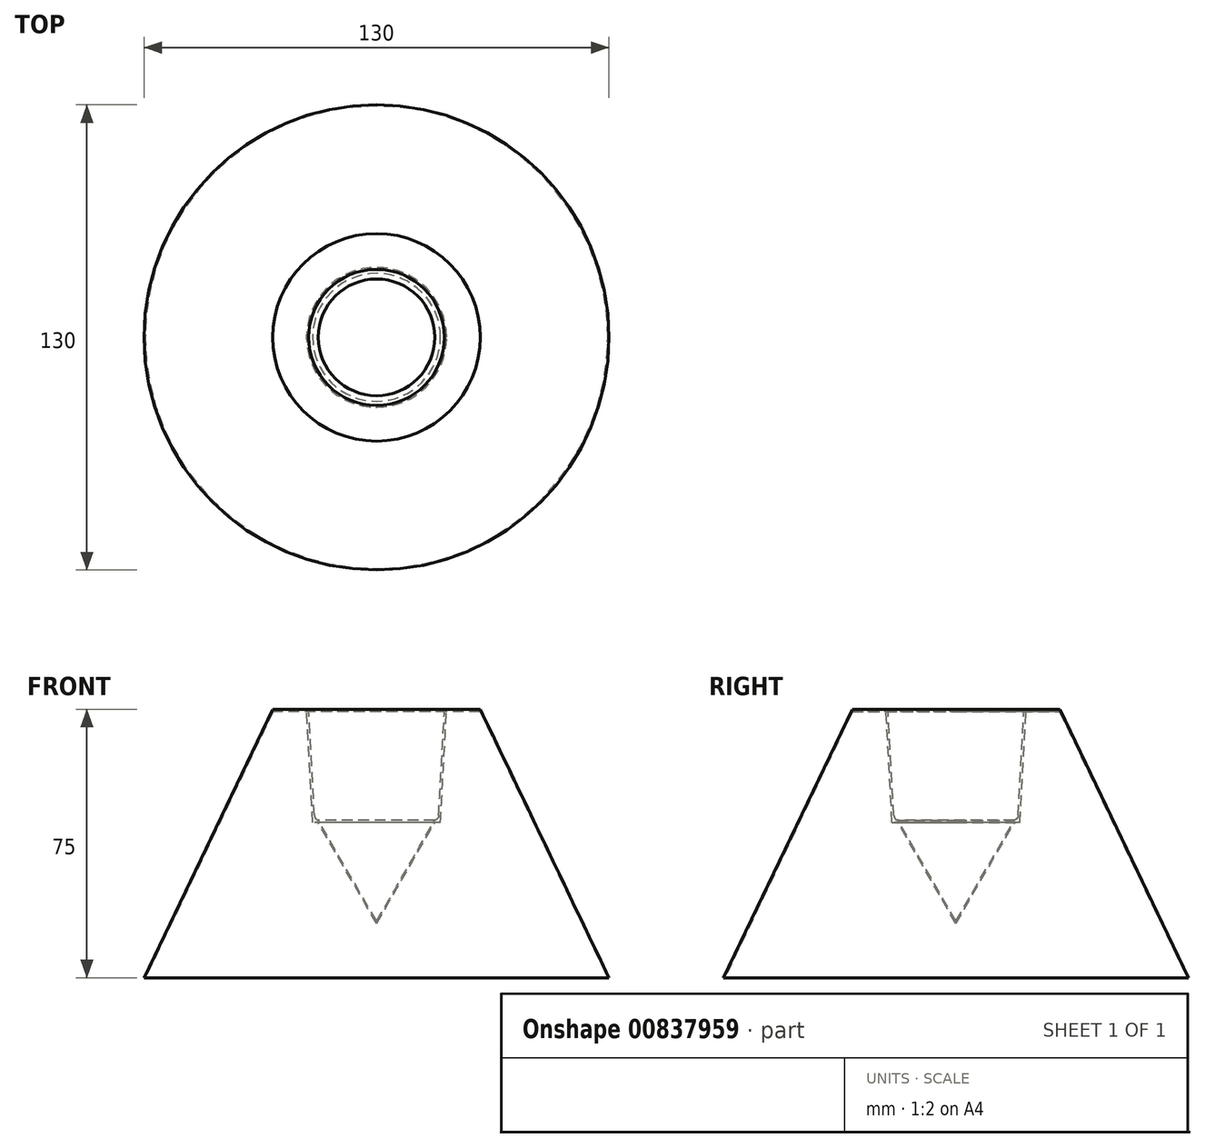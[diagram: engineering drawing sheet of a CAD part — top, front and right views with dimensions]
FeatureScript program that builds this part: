
annotation { "Feature Type Name" : "Feature", "Feature Type Description" : "" }
export const myFeature = defineFeature(function(context is Context, id is Id, definition is map)
    precondition{}
    {
        {
            var Q0;
            Q0=qCreatedBy(makeId("Front.planeOp"),FACE);
            var sketch = newSketch(context, id + "F0", { "sketchPlane" : qUnion([Q0])});
            skLineSegment(sketch, "E0", {"start": v(65, 0) * mm, "end": v(29, 75) * mm});
            skLineSegment(sketch, "E1", {"start": v(29, 75) * mm, "end": v(19, 75) * mm});
            skLineSegment(sketch, "E2", {"start": v(19, 75) * mm, "end": v(17.3, 44) * mm});
            skLineSegment(sketch, "E3", {"start": v(0, 0) * mm, "end": v(0, 1.5) * mm});
            skLineSegment(sketch, "E4", {"start": v(64.67, 0) * mm, "end": v(28.96, 74.4) * mm});
            skLineSegment(sketch, "E5", {"start": v(28.96, 74.4) * mm, "end": v(19.57, 74.4) * mm});
            skLineSegment(sketch, "E6", {"start": v(19.57, 74.4) * mm, "end": v(17.87, 43.4) * mm});
            skLineSegment(sketch, "E7", {"start": v(17.3, 44) * mm, "end": v(16.3, 44) * mm});
            skLineSegment(sketch, "E8", {"start": v(16.3, 44) * mm, "end": v(0, 15.77) * mm});
            skLineSegment(sketch, "E9", {"start": v(17.87, 43.4) * mm, "end": v(16.3, 43.4) * mm});
            skLineSegment(sketch, "E10", {"start": v(16.3, 43.4) * mm, "end": v(0, 15.17) * mm});
            skLineSegment(sketch, "E11", {"start": v(0, 71.23) * mm, "end": v(0, 15.77) * mm, "construction": true});
            skLineSegment(sketch, "E12", {"start": v(0, 15.77) * mm, "end": v(0, 15.17) * mm});
            skLineSegment(sketch, "E13.trimOffspring", {"start": v(0, 15.17) * mm, "end": v(0, -16.2) * mm, "construction": true});
            skLineSegment(sketch, "E14", {"start": v(64.67, 0) * mm, "end": v(65, 0) * mm});
            skPoint(sketch, "E15.end.orphan", {"position": v(25, 0) * mm});
            skPoint(sketch, "E16.orphan", {"position": v(0, 30.02) * mm});
            skSolve(sketch);
        }
        {
            var Q0;
            Q0=makeQuery(id+"F0.imprint","IMPRINT",FACE,{"disambiguationData":[TD([[makeQuery(id+"F0.imprint","IMPRINT",EDGE,{"derivedFrom":sQuery(id+"F0.wireOp",EDGE,"E0")}),1.0]])]});
            var Q1;
            Q1=sQuery(id+"F0.wireOp",EDGE,"E11");
            revolve(context, id + "F1", {"surfaceOperationType" : NewSurfaceOperationType.NEW, "entities" : qUnion([Q0]), "axis" : qUnion([Q1]), "revolveType" : RevolveType.ONE_DIRECTION, "angle" : 360 * degree});
        }
        {
            var Q0;
            Q0=makeQuery(id+"F1.opRevolve","SWEPT_EDGE",EDGE,{"disambiguationData":[OSD([sQuery(id+"F0.wireOp",EDGE,"E2"),sQuery(id+"F0.wireOp",EDGE,"E7")])]});
            fillet(context, id + "F2", {"entities" : qUnion([Q0]), "radius" : 1.5 * mm, "tangentPropagation" : true, "allowEdgeOverflow" : false});
        }
    });
